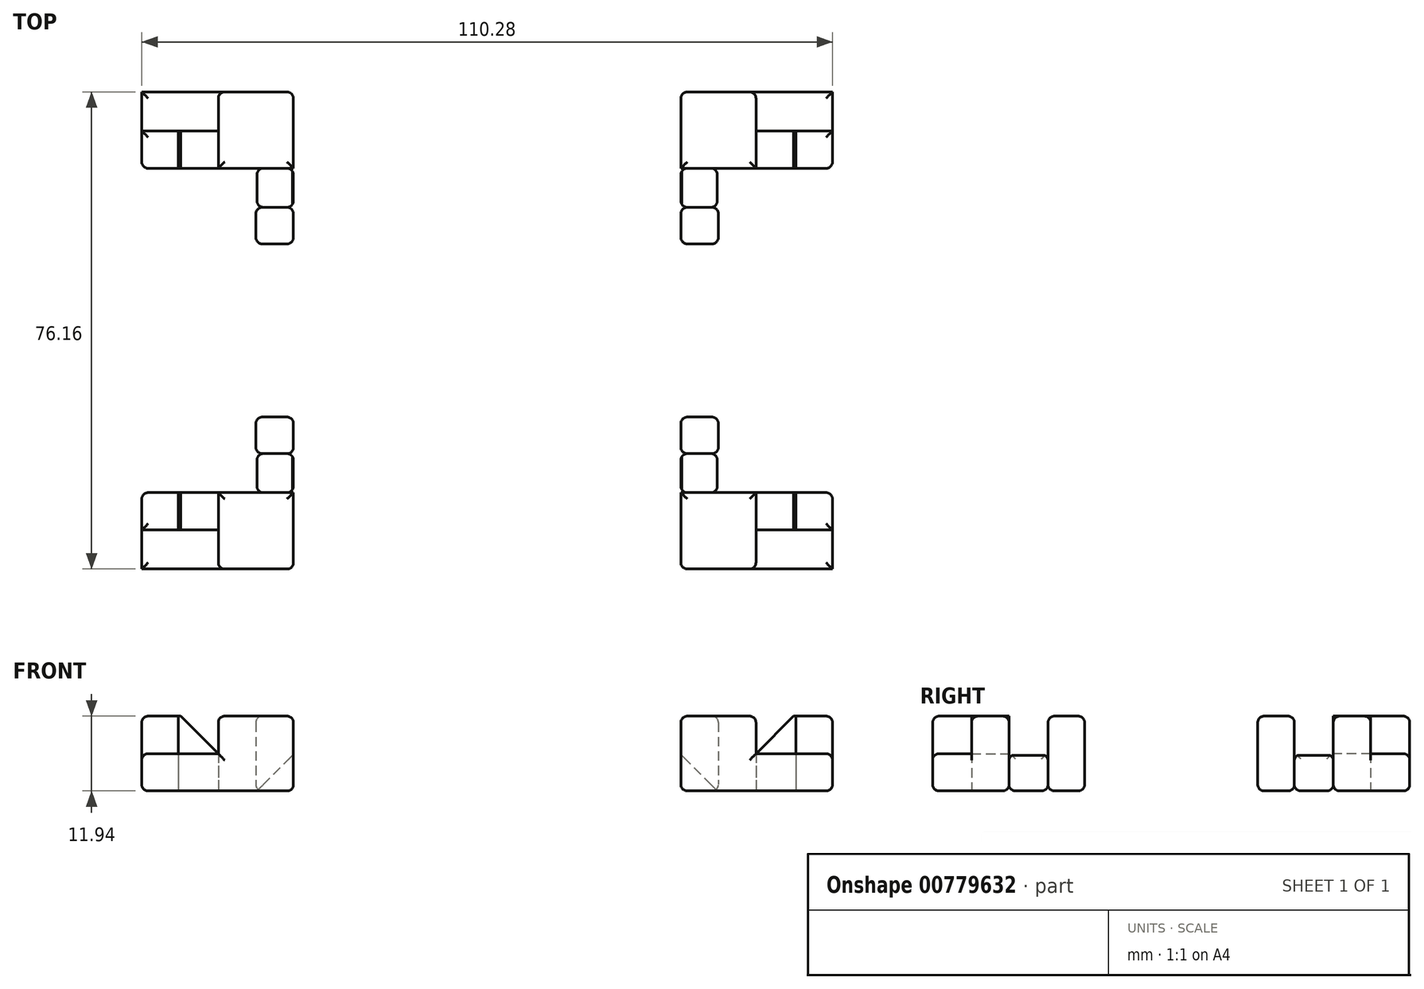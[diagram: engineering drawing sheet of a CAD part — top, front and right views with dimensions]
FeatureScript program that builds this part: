
annotation { "Feature Type Name" : "Feature", "Feature Type Description" : "" }
export const myFeature = defineFeature(function(context is Context, id is Id, definition is map)
    precondition{}
    {
        {
            var Q0;
            Q0=qCreatedBy(makeId("Top.planeOp"),FACE);
            var sketch = newSketch(context, id + "F0", { "sketchPlane" : qUnion([Q0])});
            skLineSegment(sketch, "E0.top", {"start": v(-55.14, 25.9) * mm, "end": v(-36.93, 25.9) * mm});
            skLineSegment(sketch, "E0.left", {"start": v(-55.14, 38.08) * mm, "end": v(-55.14, 25.9) * mm});
            skLineSegment(sketch, "E1.top", {"start": v(-36.93, 13.83) * mm, "end": v(-30.94, 13.83) * mm});
            skLineSegment(sketch, "E1.left", {"start": v(-36.93, 25.9) * mm, "end": v(-36.93, 13.83) * mm});
            skLineSegment(sketch, "E1.right", {"start": v(-30.94, 38.08) * mm, "end": v(-30.94, 13.83) * mm});
            skLineSegment(sketch, "E2", {"start": v(-30.94, 38.08) * mm, "end": v(-55.14, 38.08) * mm});
            skLineSegment(sketch, "E3", {"start": v(-42.93, 38.08) * mm, "end": v(-42.93, 25.9) * mm});
            skLineSegment(sketch, "E4", {"start": v(-36.93, 19.67) * mm, "end": v(-30.94, 19.67) * mm});
            skLineSegment(sketch, "E5", {"start": v(-36.93, 25.9) * mm, "end": v(-30.94, 25.9) * mm});
            skLineSegment(sketch, "E6", {"start": v(-55.14, 31.86) * mm, "end": v(-49.3, 31.86) * mm});
            skLineSegment(sketch, "E7", {"start": v(-49.3, 31.86) * mm, "end": v(-49.3, 25.9) * mm});
            skLineSegment(sketch, "E8", {"start": v(-49.3, 31.86) * mm, "end": v(-42.93, 31.86) * mm});
            skPoint(sketch, "E8.endSnap0", {"position": v(-42.93, 31.99) * mm});
            skSolve(sketch);
        }
        {
            var Q0;
            {var subQ4=sQuery(id+"F0.wireOp",EDGE,"E6");Q0=makeQuery(id+"F0.imprint","IMPRINT",FACE,{"disambiguationData":[TD([[makeQuery(id+"F0.imprint","IMPRINT",EDGE,{"derivedFrom":subQ4}),-1.0]])]});}
            var Q1;
            {var subQ6=sQuery(id+"F0.wireOp",EDGE,"E5");Q1=makeQuery(id+"F0.imprint","IMPRINT",FACE,{"disambiguationData":[TD([[makeQuery(id+"F0.imprint","IMPRINT",EDGE,{"derivedFrom":subQ6}),1.0]])]});}
            var Q2;
            {var subQ0=sQuery(id+"F0.wireOp",EDGE,"E1.top");Q2=makeQuery(id+"F0.imprint","IMPRINT",FACE,{"disambiguationData":[TD([[makeQuery(id+"F0.imprint","IMPRINT",EDGE,{"derivedFrom":subQ0}),1.0]])]});}
            extrude(context, id + "F1", {"entities" : qUnion([Q0, Q1, Q2]), "depth" : 11.94 * mm, "offsetDistance" : 25.4 * mm});
        }
        {
            var Q0;
            {var subQ0=sQuery(id+"F0.wireOp",EDGE,"E6");Q0=makeQuery(id+"F0.imprint","IMPRINT",FACE,{"disambiguationData":[TD([[makeQuery(id+"F0.imprint","IMPRINT",EDGE,{"derivedFrom":subQ0}),1.0]])]});}
            extrude(context, id + "F2", {"entities" : qUnion([Q0]), "operationType" : NewBodyOperationType.ADD, "depth" : 5.94 * mm, "offsetDistance" : 25.4 * mm});
        }
        {
            var Q0;
            {var subQ2=sQuery(id+"F0.wireOp",EDGE,"E4");Q0=makeQuery(id+"F0.imprint","IMPRINT",FACE,{"disambiguationData":[TD([[makeQuery(id+"F0.imprint","IMPRINT",EDGE,{"derivedFrom":subQ2}),1.0]])]});}
            var Q1;
            Q1 = qSketchRegion(id + "FC75VdvWWpckfvP_1", true);
            extrude(context, id + "F3", {"entities" : qUnion([Q0, Q1]), "depth" : 5.66 * mm, "offsetDistance" : 25.4 * mm});
        }
        {
            var Q0;
            Q0=makeQuery(id+"F3.opExtrude","CAP_EDGE",EDGE,{"disambiguationData":[OSD([sQuery(id+"F0.wireOp",EDGE,"E1.left")])],"isStart":false});
            chamfer(context, id + "F4", {"entities" : qUnion([Q0]), "width" : 5.84 * mm, "tangentPropagation" : true});
        }
        {
            var Q0;
            {var subQ3=sQuery(id+"F0.wireOp",EDGE,"E7");Q0=makeQuery(id+"F0.imprint","IMPRINT",FACE,{"disambiguationData":[TD([[makeQuery(id+"F0.imprint","IMPRINT",EDGE,{"derivedFrom":subQ3}),1.0]])]});}
            var Q1;
            Q1=makeQuery(id+"F1.opExtrude","CAP_FACE",FACE,{"disambiguationData":[OSD([sQuery(id+"F0.wireOp",EDGE,"E0.top"),sQuery(id+"F0.wireOp",EDGE,"E0.left"),sQuery(id+"F0.wireOp",EDGE,"E6"),sQuery(id+"F0.wireOp",EDGE,"E7")])],"isStart":false});
            extrude(context, id + "F5", {"entities" : qUnion([Q0]), "endBound" : BoundingType.UP_TO_SURFACE, "depth" : 25.4 * mm, "endBoundEntityFace" : qUnion([Q1]), "offsetDistance" : 25.4 * mm});
        }
        {
            var Q0;
            Q0=makeQuery(id+"F5.opExtrude","CAP_EDGE",EDGE,{"disambiguationData":[OSD([sQuery(id+"F0.wireOp",EDGE,"E3")])],"isStart":false});
            chamfer(context, id + "F6", {"entities" : qUnion([Q0]), "width" : 6 * mm, "tangentPropagation" : true});
        }
        {
            var Q0;
            Q0=makeQuery(id+"F1.opExtrude","SWEPT_EDGE",EDGE,{"disambiguationData":[OSD([sQuery(id+"F0.wireOp",EDGE,"E1.top"),sQuery(id+"F0.wireOp",EDGE,"E1.left")])]});
            var Q1;
            Q1=makeQuery(id+"F1.opExtrude","CAP_EDGE",EDGE,{"disambiguationData":[OSD([sQuery(id+"F0.wireOp",EDGE,"E1.left")])],"isStart":false});
            var Q2;
            Q2=makeQuery(id+"F1.opExtrude","CAP_EDGE",EDGE,{"disambiguationData":[OSD([sQuery(id+"F0.wireOp",EDGE,"E1.top")])],"isStart":false});
            var Q3;
            {var subQ0=sQuery(id+"F0.wireOp",EDGE,"E1.right");Q3=makeQuery(id+"F1.opExtrude","CAP_EDGE",EDGE,{"disambiguationData":[OSD([subQ0]),TDD([makeQuery(id+"F0.imprint","IMPRINT",EDGE,{"disambiguationData":[TD([[makeQuery(id+"F0.imprint","INTERSECT",VERTEX,{"derivedFrom":[sQuery(id+"F0.wireOp",EDGE,"E1.top"),subQ0]}),1.0]])],"derivedFrom":subQ0})])],"isStart":false});}
            var Q4;
            Q4=makeQuery(id+"F1.opExtrude","CAP_EDGE",EDGE,{"disambiguationData":[OSD([sQuery(id+"F0.wireOp",EDGE,"E4")])],"isStart":false});
            var Q5;
            Q5=makeQuery(id+"F1.opExtrude","CAP_EDGE",EDGE,{"disambiguationData":[OSD([sQuery(id+"F0.wireOp",EDGE,"E6")])],"isStart":false});
            var Q6;
            Q6=makeQuery(id+"F1.opExtrude","CAP_EDGE",EDGE,{"disambiguationData":[OSD([sQuery(id+"F0.wireOp",EDGE,"E0.top")])],"isStart":false});
            var Q7;
            Q7=makeQuery(id+"F1.opExtrude","CAP_EDGE",EDGE,{"disambiguationData":[OSD([sQuery(id+"F0.wireOp",EDGE,"E0.left")])],"isStart":false});
            var Q8;
            Q8=makeQuery(id+"F1.opExtrude","SWEPT_EDGE",EDGE,{"disambiguationData":[OSD([sQuery(id+"F0.wireOp",EDGE,"E0.top"),sQuery(id+"F0.wireOp",EDGE,"E0.left")])]});
            var Q9;
            Q9=makeQuery(id+"F2.opExtrude","CAP_EDGE",EDGE,{"disambiguationData":[OSD([sQuery(id+"F0.wireOp",EDGE,"E0.left")])],"isStart":false});
            var Q10;
            Q10=makeQuery(id+"F2.opExtrude","CAP_EDGE",EDGE,{"disambiguationData":[OSD([sQuery(id+"F0.wireOp",EDGE,"E0.left")])],"isStart":true});
            var Q11;
            Q11=makeQuery(id+"F2.opExtrude","CAP_EDGE",EDGE,{"disambiguationData":[OSD([sQuery(id+"F0.wireOp",EDGE,"E2")])],"isStart":false});
            var Q12;
            Q12=makeQuery(id+"F1.opExtrude","CAP_EDGE",EDGE,{"disambiguationData":[OSD([sQuery(id+"F0.wireOp",EDGE,"E3")])],"isStart":false});
            var Q13;
            Q13=makeQuery(id+"F1.opExtrude","CAP_EDGE",EDGE,{"disambiguationData":[OSD([sQuery(id+"F0.wireOp",EDGE,"E2")])],"isStart":false});
            var Q14;
            Q14=makeQuery(id+"F1.opExtrude","SWEPT_EDGE",EDGE,{"disambiguationData":[OSD([sQuery(id+"F0.wireOp",EDGE,"E2"),sQuery(id+"F0.wireOp",EDGE,"E3")])]});
            var Q15;
            {var subQ0=sQuery(id+"F0.wireOp",EDGE,"E2");Q15=makeQuery(id+"F2.boolean.opBoolean","MERGE",EDGE,{"derivedFrom":[makeQuery(id+"F1.opExtrude","CAP_EDGE",EDGE,{"disambiguationData":[OSD([subQ0])],"isStart":true}),makeQuery(id+"F2.opExtrude","CAP_EDGE",EDGE,{"disambiguationData":[OSD([subQ0])],"isStart":true})]});}
            var Q16;
            Q16=makeQuery(id+"F1.opExtrude","CAP_EDGE",EDGE,{"disambiguationData":[OSD([sQuery(id+"F0.wireOp",EDGE,"E0.top"),sQuery(id+"F0.wireOp",EDGE,"E5")])],"isStart":false});
            var Q17;
            {var subQ0=sQuery(id+"F0.wireOp",EDGE,"E1.right");Q17=makeQuery(id+"F1.opExtrude","CAP_EDGE",EDGE,{"disambiguationData":[OSD([subQ0]),TDD([makeQuery(id+"F0.imprint","IMPRINT",EDGE,{"disambiguationData":[TD([[makeQuery(id+"F0.imprint","INTERSECT",VERTEX,{"derivedFrom":[subQ0,sQuery(id+"F0.wireOp",EDGE,"E2")]}),-1.0]])],"derivedFrom":subQ0})])],"isStart":false});}
            var Q18;
            Q18=makeQuery(id+"F1.opExtrude","SWEPT_EDGE",EDGE,{"disambiguationData":[OSD([sQuery(id+"F0.wireOp",EDGE,"E1.right"),sQuery(id+"F0.wireOp",EDGE,"E2")])]});
            var Q19;
            {var subQ0=sQuery(id+"F0.wireOp",EDGE,"E1.right");Q19=makeQuery(id+"F1.opExtrude","CAP_EDGE",EDGE,{"disambiguationData":[OSD([subQ0]),TDD([makeQuery(id+"F0.imprint","IMPRINT",EDGE,{"disambiguationData":[TD([[makeQuery(id+"F0.imprint","INTERSECT",VERTEX,{"derivedFrom":[subQ0,sQuery(id+"F0.wireOp",EDGE,"E2")]}),-1.0]])],"derivedFrom":subQ0})])],"isStart":true});}
            var Q20;
            Q20=makeQuery(id+"F1.opExtrude","SWEPT_EDGE",EDGE,{"disambiguationData":[OSD([sQuery(id+"F0.wireOp",EDGE,"E1.top"),sQuery(id+"F0.wireOp",EDGE,"E1.right")])]});
            var Q21;
            Q21=makeQuery(id+"F1.opExtrude","SWEPT_EDGE",EDGE,{"disambiguationData":[OSD([sQuery(id+"F0.wireOp",EDGE,"E1.left"),sQuery(id+"F0.wireOp",EDGE,"E4")])]});
            var Q22;
            Q22=makeQuery(id+"F3.opExtrude","CAP_EDGE",EDGE,{"disambiguationData":[OSD([sQuery(id+"F0.wireOp",EDGE,"E1.right")])],"isStart":true});
            var Q23;
            {var subQ0=sQuery(id+"F0.wireOp",EDGE,"E1.right");Q23=makeQuery(id+"F1.opExtrude","CAP_EDGE",EDGE,{"disambiguationData":[OSD([subQ0]),TDD([makeQuery(id+"F0.imprint","IMPRINT",EDGE,{"disambiguationData":[TD([[makeQuery(id+"F0.imprint","INTERSECT",VERTEX,{"derivedFrom":[sQuery(id+"F0.wireOp",EDGE,"E1.top"),subQ0]}),1.0]])],"derivedFrom":subQ0})])],"isStart":true});}
            var Q24;
            Q24=makeQuery(id+"F1.opExtrude","CAP_EDGE",EDGE,{"disambiguationData":[OSD([sQuery(id+"F0.wireOp",EDGE,"E1.top")])],"isStart":true});
            var Q25;
            Q25=makeQuery(id+"F1.opExtrude","CAP_EDGE",EDGE,{"disambiguationData":[OSD([sQuery(id+"F0.wireOp",EDGE,"E1.left")])],"isStart":true});
            var Q26;
            Q26=makeQuery(id+"F1.opExtrude","CAP_EDGE",EDGE,{"disambiguationData":[OSD([sQuery(id+"F0.wireOp",EDGE,"E0.left")])],"isStart":true});
            var Q27;
            Q27=makeQuery(id+"F1.opExtrude","CAP_EDGE",EDGE,{"disambiguationData":[OSD([sQuery(id+"F0.wireOp",EDGE,"E0.top")])],"isStart":true});
            var Q28;
            Q28=makeQuery(id+"F5.opExtrude","CAP_EDGE",EDGE,{"disambiguationData":[OSD([sQuery(id+"F0.wireOp",EDGE,"E0.top")])],"isStart":true});
            var Q29;
            Q29=makeQuery(id+"F1.opExtrude","CAP_EDGE",EDGE,{"disambiguationData":[OSD([sQuery(id+"F0.wireOp",EDGE,"E0.top"),sQuery(id+"F0.wireOp",EDGE,"E5")])],"isStart":true});
            fillet(context, id + "F7", {"entities" : qUnion([Q0, Q1, Q2, Q3, Q4, Q5, Q6, Q7, Q8, Q9, Q10, Q11, Q12, Q13, Q14, Q15, Q16, Q17, Q18, Q19, Q20, Q21, Q22, Q23, Q24, Q25, Q26, Q27, Q28, Q29]), "radius" : 1.02 * mm, "tangentPropagation" : true, "allowEdgeOverflow" : false});
        }
        {
            var Q0;
            Q0=makeQuery(id+"F1.opExtrude","CAP_FACE",FACE,{"disambiguationData":[OSD([sQuery(id+"F0.wireOp",EDGE,"E0.top"),sQuery(id+"F0.wireOp",EDGE,"E1.right"),sQuery(id+"F0.wireOp",EDGE,"E2"),sQuery(id+"F0.wireOp",EDGE,"E3"),sQuery(id+"F0.wireOp",EDGE,"E5")])],"isStart":false});
            var Q1;
            {var subQ0=sQuery(id+"F0.wireOp",EDGE,"E2");Q1=makeQuery(id+"F2.boolean.opBoolean","MERGE",FACE,{"derivedFrom":[makeQuery(id+"F1.opExtrude","SWEPT_FACE",FACE,{"disambiguationData":[OSD([subQ0])]}),makeQuery(id+"F2.opExtrude","SWEPT_FACE",FACE,{"disambiguationData":[OSD([subQ0])]})]});}
            var Q2;
            {var subQ0=sQuery(id+"F0.wireOp",EDGE,"E1.right");Q2=makeQuery(id+"F1.opExtrude","SWEPT_FACE",FACE,{"disambiguationData":[OSD([subQ0]),TDD([makeQuery(id+"F0.imprint","IMPRINT",EDGE,{"disambiguationData":[TD([[makeQuery(id+"F0.imprint","INTERSECT",VERTEX,{"derivedFrom":[sQuery(id+"F0.wireOp",EDGE,"E1.top"),subQ0]}),1.0]])],"derivedFrom":subQ0})])]});}
            var Q3;
            Q3=makeQuery(id+"F1.opExtrude","SWEPT_FACE",FACE,{"disambiguationData":[OSD([sQuery(id+"F0.wireOp",EDGE,"E1.top")])]});
            var Q4;
            Q4=makeQuery(id+"F1.opExtrude","SWEPT_FACE",FACE,{"disambiguationData":[OSD([sQuery(id+"F0.wireOp",EDGE,"E1.left")])]});
            var Q5;
            Q5=makeQuery(id+"F1.opExtrude","CAP_EDGE",EDGE,{"disambiguationData":[OSD([sQuery(id+"F0.wireOp",EDGE,"E4")])],"isStart":false});
            var Q6;
            Q6=makeQuery(id+"F3.opExtrude","SWEPT_FACE",FACE,{"disambiguationData":[OSD([sQuery(id+"F0.wireOp",EDGE,"E1.right")])]});
            var Q7;
            Q7=makeQuery(id+"F1.opExtrude","CAP_EDGE",EDGE,{"disambiguationData":[OSD([sQuery(id+"F0.wireOp",EDGE,"E6")])],"isStart":false});
            var Q8;
            Q8=makeQuery(id+"F1.opExtrude","SWEPT_EDGE",EDGE,{"disambiguationData":[OSD([sQuery(id+"F0.wireOp",EDGE,"E6"),sQuery(id+"F0.wireOp",EDGE,"E7"),sQuery(id+"F0.wireOp",EDGE,"E8")])]});
            var Q9;
            Q9=makeQuery(id+"F1.opExtrude","CAP_FACE",FACE,{"disambiguationData":[OSD([sQuery(id+"F0.wireOp",EDGE,"E0.top"),sQuery(id+"F0.wireOp",EDGE,"E0.left"),sQuery(id+"F0.wireOp",EDGE,"E6"),sQuery(id+"F0.wireOp",EDGE,"E7")])],"isStart":false});
            var Q10;
            Q10=makeQuery(id+"F2.opExtrude","SWEPT_FACE",FACE,{"disambiguationData":[OSD([sQuery(id+"F0.wireOp",EDGE,"E0.left")])]});
            var Q11;
            Q11=makeQuery(id+"F2.opExtrude","CAP_FACE",FACE,{"disambiguationData":[OSD([sQuery(id+"F0.wireOp",EDGE,"E0.left"),sQuery(id+"F0.wireOp",EDGE,"E2"),sQuery(id+"F0.wireOp",EDGE,"E3"),sQuery(id+"F0.wireOp",EDGE,"E6"),sQuery(id+"F0.wireOp",EDGE,"E8")])],"isStart":false});
            var Q12;
            Q12=makeQuery(id+"F1.opExtrude","SWEPT_FACE",FACE,{"disambiguationData":[OSD([sQuery(id+"F0.wireOp",EDGE,"E0.top"),sQuery(id+"F0.wireOp",EDGE,"E5")])]});
            var Q13;
            Q13=makeQuery(id+"F1.opExtrude","CAP_EDGE",EDGE,{"disambiguationData":[OSD([sQuery(id+"F0.wireOp",EDGE,"E7")])],"isStart":false});
            var Q14;
            Q14=makeQuery(id+"F2.opExtrude","CAP_EDGE",EDGE,{"disambiguationData":[OSD([sQuery(id+"F0.wireOp",EDGE,"E3")])],"isStart":false});
            fillet(context, id + "F8", {"entities" : qUnion([Q0, Q1, Q2, Q3, Q4, Q5, Q6, Q7, Q8, Q9, Q10, Q11, Q12, Q13, Q14]), "radius" : 1.02 * mm, "tangentPropagation" : true, "allowEdgeOverflow" : false});
        }
        {
            var Q0;
            Q0=makeQuery(id+"F1.opExtrude","SWEPT_BODY",BODY,{"disambiguationData":[OSD([sQuery(id+"F0.wireOp",EDGE,"E0.top"),sQuery(id+"F0.wireOp",EDGE,"E0.left"),sQuery(id+"F0.wireOp",EDGE,"E6"),sQuery(id+"F0.wireOp",EDGE,"E7")])]});
            var Q1;
            Q1=makeQuery(id+"F1.opExtrude","SWEPT_BODY",BODY,{"disambiguationData":[OSD([sQuery(id+"F0.wireOp",EDGE,"E0.top"),sQuery(id+"F0.wireOp",EDGE,"E1.right"),sQuery(id+"F0.wireOp",EDGE,"E2"),sQuery(id+"F0.wireOp",EDGE,"E3"),sQuery(id+"F0.wireOp",EDGE,"E5")])]});
            var Q2;
            Q2=makeQuery(id+"F1.opExtrude","SWEPT_BODY",BODY,{"disambiguationData":[OSD([sQuery(id+"F0.wireOp",EDGE,"E1.top"),sQuery(id+"F0.wireOp",EDGE,"E1.left"),sQuery(id+"F0.wireOp",EDGE,"E1.right"),sQuery(id+"F0.wireOp",EDGE,"E4")])]});
            var Q3;
            Q3=makeQuery(id+"F3.opExtrude","SWEPT_BODY",BODY,{"disambiguationData":[OSD([sQuery(id+"F0.wireOp",EDGE,"E1.left"),sQuery(id+"F0.wireOp",EDGE,"E1.right"),sQuery(id+"F0.wireOp",EDGE,"E4"),sQuery(id+"F0.wireOp",EDGE,"E5")])]});
            var Q4;
            Q4=makeQuery(id+"F5.opExtrude","SWEPT_BODY",BODY,{"disambiguationData":[OSD([sQuery(id+"F0.wireOp",EDGE,"E0.top"),sQuery(id+"F0.wireOp",EDGE,"E3"),sQuery(id+"F0.wireOp",EDGE,"E7"),sQuery(id+"F0.wireOp",EDGE,"E8")])]});
            var Q5;
            Q5=qCreatedBy(makeId("Right.planeOp"),FACE);
            mirror(context, id + "F9", {"entities" : qUnion([Q0, Q1, Q2, Q3, Q4]), "mirrorPlane" : qUnion([Q5])});
        }
        {
            var Q0;
            Q0=makeQuery(id+"F1.opExtrude","SWEPT_BODY",BODY,{"disambiguationData":[OSD([sQuery(id+"F0.wireOp",EDGE,"E0.top"),sQuery(id+"F0.wireOp",EDGE,"E0.left"),sQuery(id+"F0.wireOp",EDGE,"E6"),sQuery(id+"F0.wireOp",EDGE,"E7")])]});
            var Q1;
            Q1=makeQuery(id+"F1.opExtrude","SWEPT_BODY",BODY,{"disambiguationData":[OSD([sQuery(id+"F0.wireOp",EDGE,"E0.top"),sQuery(id+"F0.wireOp",EDGE,"E1.right"),sQuery(id+"F0.wireOp",EDGE,"E2"),sQuery(id+"F0.wireOp",EDGE,"E3"),sQuery(id+"F0.wireOp",EDGE,"E5")])]});
            var Q2;
            Q2=makeQuery(id+"F1.opExtrude","SWEPT_BODY",BODY,{"disambiguationData":[OSD([sQuery(id+"F0.wireOp",EDGE,"E1.top"),sQuery(id+"F0.wireOp",EDGE,"E1.left"),sQuery(id+"F0.wireOp",EDGE,"E1.right"),sQuery(id+"F0.wireOp",EDGE,"E4")])]});
            var Q3;
            Q3=makeQuery(id+"F3.opExtrude","SWEPT_BODY",BODY,{"disambiguationData":[OSD([sQuery(id+"F0.wireOp",EDGE,"E1.left"),sQuery(id+"F0.wireOp",EDGE,"E1.right"),sQuery(id+"F0.wireOp",EDGE,"E4"),sQuery(id+"F0.wireOp",EDGE,"E5")])]});
            var Q4;
            Q4=makeQuery(id+"F5.opExtrude","SWEPT_BODY",BODY,{"disambiguationData":[OSD([sQuery(id+"F0.wireOp",EDGE,"E0.top"),sQuery(id+"F0.wireOp",EDGE,"E3"),sQuery(id+"F0.wireOp",EDGE,"E7"),sQuery(id+"F0.wireOp",EDGE,"E8")])]});
            var Q5;
            Q5=makeQuery(id+"F9.opPattern","COPY",BODY,{"derivedFrom":makeQuery(id+"F3.opExtrude","SWEPT_BODY",BODY,{"disambiguationData":[OSD([sQuery(id+"F0.wireOp",EDGE,"E1.left"),sQuery(id+"F0.wireOp",EDGE,"E1.right"),sQuery(id+"F0.wireOp",EDGE,"E4"),sQuery(id+"F0.wireOp",EDGE,"E5")])]}),"instanceName":"1"});
            var Q6;
            Q6=makeQuery(id+"F9.opPattern","COPY",BODY,{"derivedFrom":makeQuery(id+"F5.opExtrude","SWEPT_BODY",BODY,{"disambiguationData":[OSD([sQuery(id+"F0.wireOp",EDGE,"E0.top"),sQuery(id+"F0.wireOp",EDGE,"E3"),sQuery(id+"F0.wireOp",EDGE,"E7"),sQuery(id+"F0.wireOp",EDGE,"E8")])]}),"instanceName":"1"});
            var Q7;
            Q7=makeQuery(id+"F9.opPattern","COPY",BODY,{"derivedFrom":makeQuery(id+"F1.opExtrude","SWEPT_BODY",BODY,{"disambiguationData":[OSD([sQuery(id+"F0.wireOp",EDGE,"E1.top"),sQuery(id+"F0.wireOp",EDGE,"E1.left"),sQuery(id+"F0.wireOp",EDGE,"E1.right"),sQuery(id+"F0.wireOp",EDGE,"E4")])]}),"instanceName":"1"});
            var Q8;
            Q8=makeQuery(id+"F9.opPattern","COPY",BODY,{"derivedFrom":makeQuery(id+"F1.opExtrude","SWEPT_BODY",BODY,{"disambiguationData":[OSD([sQuery(id+"F0.wireOp",EDGE,"E0.top"),sQuery(id+"F0.wireOp",EDGE,"E1.right"),sQuery(id+"F0.wireOp",EDGE,"E2"),sQuery(id+"F0.wireOp",EDGE,"E3"),sQuery(id+"F0.wireOp",EDGE,"E5")])]}),"instanceName":"1"});
            var Q9;
            Q9=makeQuery(id+"F9.opPattern","COPY",BODY,{"derivedFrom":makeQuery(id+"F1.opExtrude","SWEPT_BODY",BODY,{"disambiguationData":[OSD([sQuery(id+"F0.wireOp",EDGE,"E0.top"),sQuery(id+"F0.wireOp",EDGE,"E0.left"),sQuery(id+"F0.wireOp",EDGE,"E6"),sQuery(id+"F0.wireOp",EDGE,"E7")])]}),"instanceName":"1"});
            var Q10;
            Q10=qCreatedBy(makeId("Front.planeOp"),FACE);
            mirror(context, id + "F10", {"entities" : qUnion([Q0, Q1, Q2, Q3, Q4, Q5, Q6, Q7, Q8, Q9]), "mirrorPlane" : qUnion([Q10])});
        }
    });
